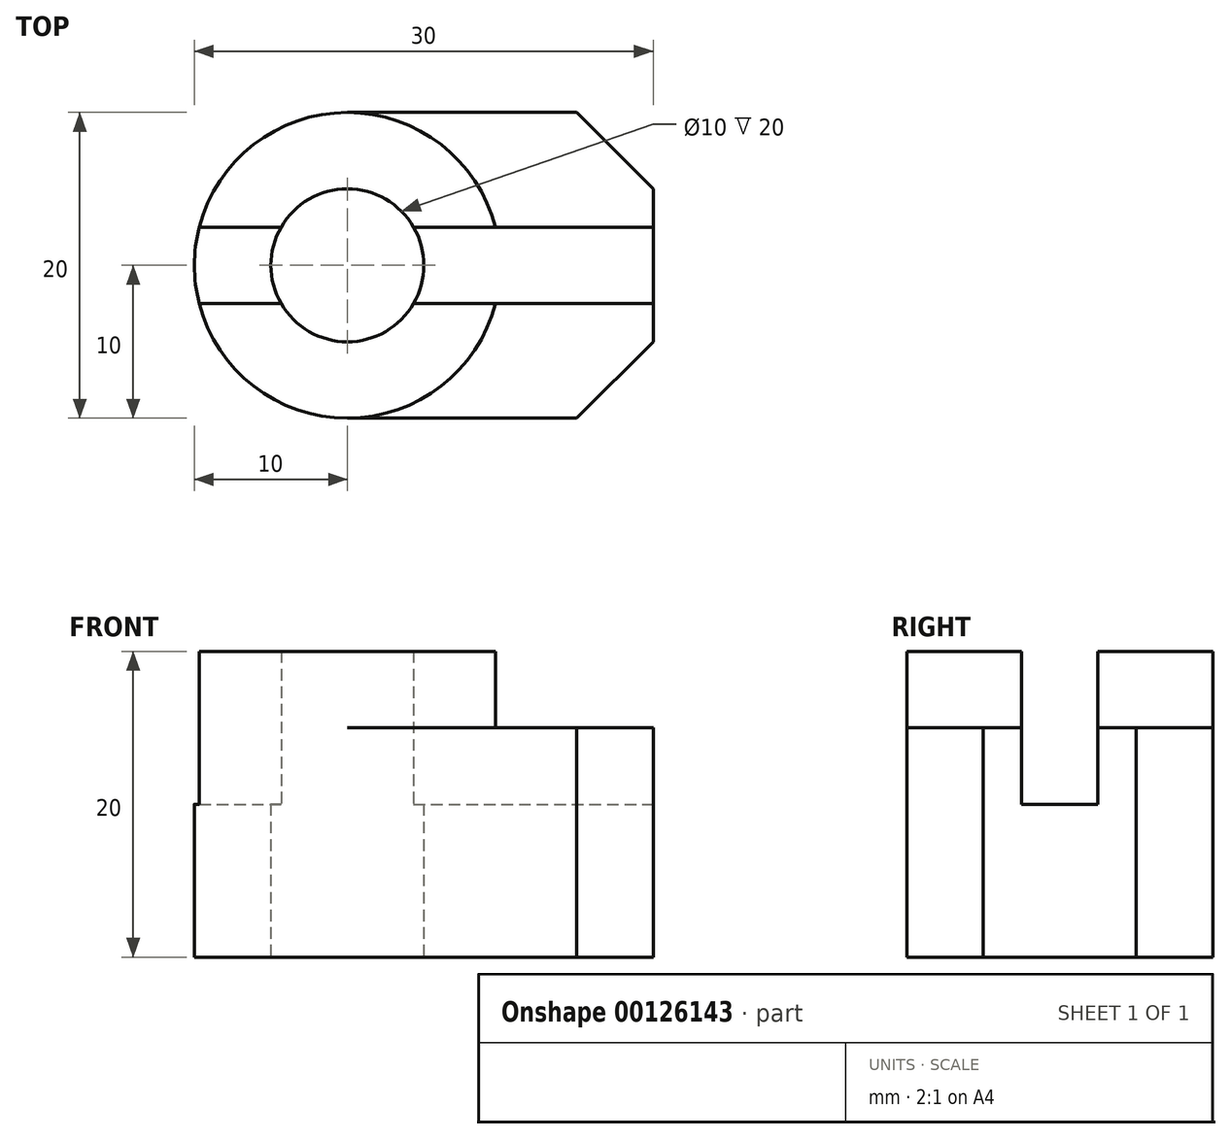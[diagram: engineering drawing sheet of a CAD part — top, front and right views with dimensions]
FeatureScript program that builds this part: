
annotation { "Feature Type Name" : "Feature", "Feature Type Description" : "" }
export const myFeature = defineFeature(function(context is Context, id is Id, definition is map)
    precondition{}
    {
        {
            var Q0;
            Q0=qCreatedBy(makeId("Top.planeOp"),FACE);
            var sketch = newSketch(context, id + "F0", { "sketchPlane" : qUnion([Q0])});
            skArc(sketch, "E0", {"start": v(0, 10) * mm, "mid": v(-10, 0) * mm, "end": v(0, -10) * mm});
            skLineSegment(sketch, "E1", {"start": v(0, 10) * mm, "end": v(15, 10) * mm});
            skLineSegment(sketch, "E2", {"start": v(15, 10) * mm, "end": v(20, 5) * mm});
            skLineSegment(sketch, "E3", {"start": v(20, 5) * mm, "end": v(20, -5) * mm});
            skLineSegment(sketch, "E4", {"start": v(0, -10) * mm, "end": v(15, -10) * mm});
            skLineSegment(sketch, "E5", {"start": v(15, -10) * mm, "end": v(20, -5) * mm});
            skCircle(sketch, "E6", {"center": v(0, 0) * mm, "radius": 5 * mm});
            skArc(sketch, "E7", {"start": v(0, -10) * mm, "mid": v(10, 0) * mm, "end": v(0, 10) * mm});
            skSolve(sketch);
        }
        {
            var Q0;
            Q0 = qSketchRegion(id + "F0", true);
            extrude(context, id + "F1", {"entities" : qUnion([Q0]), "depth" : 15 * mm});
        }
        {
            var Q0;
            Q0=makeQuery(id+"F0.imprint","IMPRINT",FACE,{"disambiguationData":[TD([[makeQuery(id+"F0.imprint","IMPRINT",EDGE,{"derivedFrom":sQuery(id+"F0.wireOp",EDGE,"E0")}),1.0]])]});
            extrude(context, id + "F2", {"entities" : qUnion([Q0]), "operationType" : NewBodyOperationType.ADD, "depth" : 20 * mm});
        }
        {
            var Q0;
            Q0=makeQuery(id+"F1.opExtrude","SWEPT_FACE",FACE,{"disambiguationData":[OSD([sQuery(id+"F0.wireOp",EDGE,"E3")])]});
            var sketch = newSketch(context, id + "F3", { "sketchPlane" : qUnion([Q0])});
            skLineSegment(sketch, "E8", {"start": v(2.5, 15) * mm, "end": v(2.5, 10) * mm});
            skLineSegment(sketch, "E9", {"start": v(2.5, 10) * mm, "end": v(-2.5, 10) * mm});
            skLineSegment(sketch, "E10", {"start": v(-2.5, 10) * mm, "end": v(-2.5, 15) * mm});
            skLineSegment(sketch, "E11", {"start": v(2.5, 15) * mm, "end": v(2.5, 20) * mm});
            skLineSegment(sketch, "E12", {"start": v(2.5, 20) * mm, "end": v(-2.5, 20) * mm});
            skLineSegment(sketch, "E13", {"start": v(-2.5, 20) * mm, "end": v(-2.5, 15) * mm});
            skSolve(sketch);
        }
        {
            var Q0;
            Q0 = qSketchRegion(id + "F3", true);
            extrude(context, id + "F4", {"entities" : qUnion([Q0]), "operationType" : NewBodyOperationType.REMOVE, "endBound" : BoundingType.THROUGH_ALL, "oppositeDirection" : true, "depth" : 25 * mm});
        }
    });
